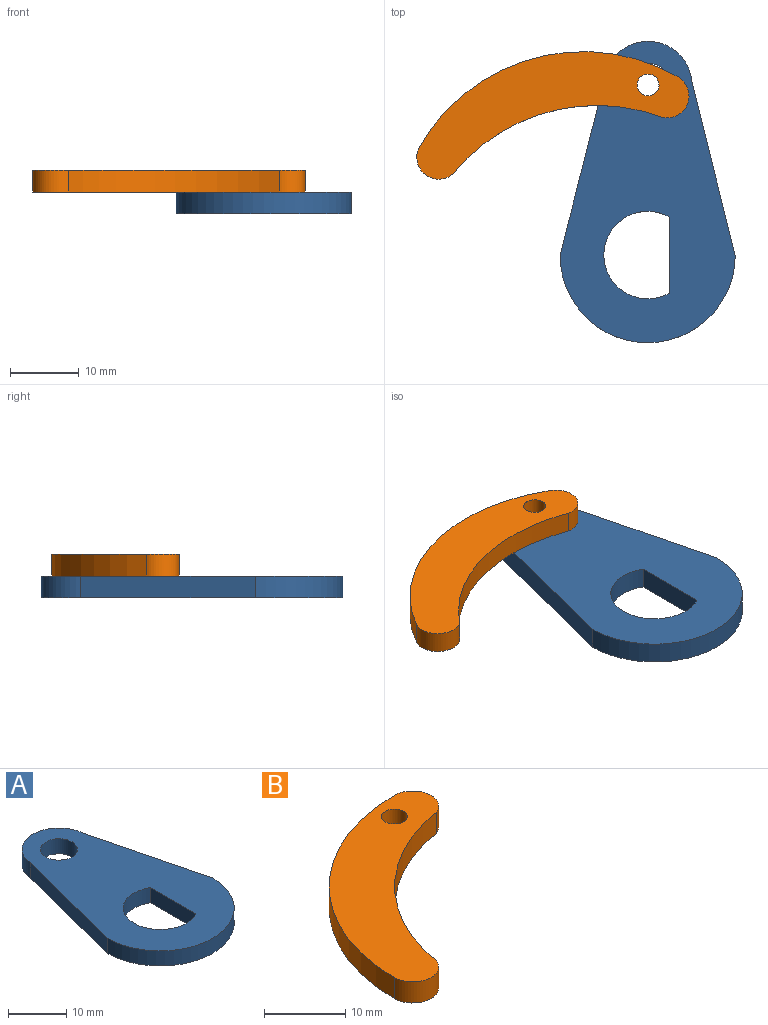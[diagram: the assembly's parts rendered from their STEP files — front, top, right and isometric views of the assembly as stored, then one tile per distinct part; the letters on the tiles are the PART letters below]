
ASSEMBLY  parts=2 mates=1
PART A: 9 faces, bbox 25.4x43.7x3.2 mm
  f0: cylinder r=6.35mm len=12.7mm, axis (0,0,1), area 84.5mm2, adj f6,f7,f8
  f1: plane 25.26x6.32mm, normal (0.97,0.24,0), area 82.7mm2, adj f2,f4,f7,f8
  f2: cylinder r=6.35mm len=12.64mm, axis (0,0,1), area 59.4mm2, adj f1,f3,f7,f8
  f3: plane 25.27x6.44mm, normal (-0.97,0.25,0), area 82.8mm2, adj f2,f4,f7,f8
  f4: cylinder r=12.7mm len=25.4mm, axis (0,0,1), area 126.7mm2, adj f1,f3,f7,f8
  f5: cylinder r=3.17mm len=6.35mm, axis (0,0,1), area 63.3mm2, adj f7,f8
  f6: plane 11x3.18mm, normal (-1,0,0), area 34.9mm2, adj f0,f7,f8
  f7: plane 43.7x25.4mm, normal (0,0,-1), area 655.9mm2, adj f0,f1,f2,f3,f4,f5,f6
  f8: plane 43.7x25.4mm, normal (0,0,1), area 655.9mm2, adj f0,f1,f2,f3,f4,f5,f6
PART B: 7 faces, bbox 30.6x30.6x3.2 mm
  f0: cylinder r=27.42mm len=27.42mm, axis (0,0,1), area 136.8mm2, adj f1,f4,f5,f6
  f1: cylinder r=3.19mm len=6.17mm, axis (0,0,1), area 28.1mm2, adj f0,f2,f5,f6
  f2: cylinder r=26.99mm len=22.38mm, axis (0,0,1), area 107.4mm2, adj f1,f4,f5,f6
  f3: cylinder r=1.59mm len=3.18mm, axis (0,0,1), area 31.7mm2, adj f5,f6
  f4: cylinder r=3.19mm len=6.17mm, axis (0,0,1), area 28.1mm2, adj f0,f2,f5,f6
  f5: plane 30.61x30.61mm, normal (0,0,-1), area 302.7mm2, adj f0,f1,f2,f3,f4
  f6: plane 30.61x30.61mm, normal (0,0,1), area 302.7mm2, adj f0,f1,f2,f3,f4
PLACE A t=(-12.77,8.42,8.11)mm
PLACE B rot(axis=(0,0,-1),30deg) t=(-20.1,3.12,11.29)mm
MATE revolute A.f2 <-> B.f3  axis (0,0,1) through (-12.71,33.07,8.11)mm
